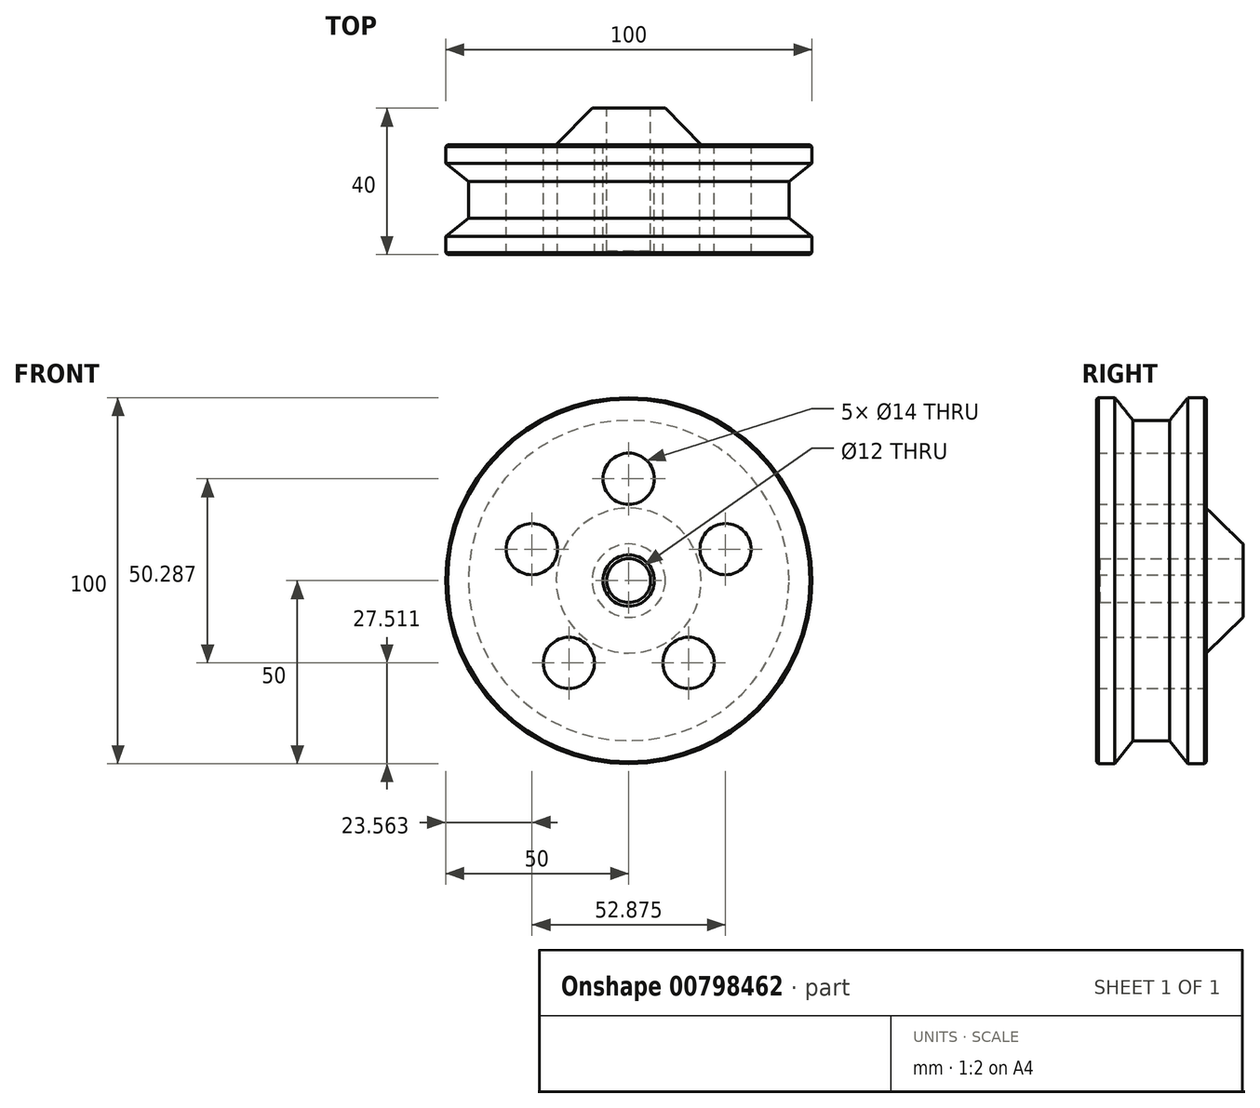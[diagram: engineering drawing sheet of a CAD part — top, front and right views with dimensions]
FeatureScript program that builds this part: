
annotation { "Feature Type Name" : "Feature", "Feature Type Description" : "" }
export const myFeature = defineFeature(function(context is Context, id is Id, definition is map)
    precondition{}
    {
        {
            var Q0;
            Q0=qCreatedBy(makeId("Top.planeOp"),FACE);
            var sketch = newSketch(context, id + "F0", { "sketchPlane" : qUnion([Q0])});
            skLineSegment(sketch, "E0.top", {"start": v(0, -40) * mm, "end": v(-50, -40) * mm});
            skLineSegment(sketch, "E0.left", {"start": v(0, 0) * mm, "end": v(0, -40) * mm});
            skLineSegment(sketch, "E1", {"start": v(-50, -10) * mm, "end": v(-50, -15) * mm});
            skLineSegment(sketch, "E2", {"start": v(-50, -15) * mm, "end": v(-43.76, -20) * mm});
            skLineSegment(sketch, "E3", {"start": v(-43.76, -20) * mm, "end": v(-43.76, -30) * mm});
            skLineSegment(sketch, "E4", {"start": v(-43.76, -30) * mm, "end": v(-50, -35) * mm});
            skLineSegment(sketch, "E5", {"start": v(-50, -40) * mm, "end": v(-50, -35) * mm});
            skLineSegment(sketch, "E6", {"start": v(0, 0) * mm, "end": v(-10, 0) * mm});
            skLineSegment(sketch, "E7", {"start": v(-10, 0) * mm, "end": v(-19.8, -10) * mm});
            skLineSegment(sketch, "E8", {"start": v(-19.8, -10) * mm, "end": v(-50, -10) * mm});
            skSolve(sketch);
        }
        {
            var Q0;
            Q0=makeQuery(id+"F0.imprint","IMPRINT",FACE,{"disambiguationData":[TD([[makeQuery(id+"F0.imprint","IMPRINT",EDGE,{"derivedFrom":sQuery(id+"F0.wireOp",EDGE,"E0.top")}),-1.0]])]});
            var Q1;
            Q1=sQuery(id+"F0.wireOp",EDGE,"E0.left");
            revolve(context, id + "F1", {"surfaceOperationType" : NewSurfaceOperationType.NEW, "entities" : qUnion([Q0]), "axis" : qUnion([Q1]), "revolveType" : RevolveType.FULL});
        }
        {
            var Q0;
            Q0=makeQuery(id+"F1.opRevolve","SWEPT_FACE",FACE,{"disambiguationData":[OSD([sQuery(id+"F0.wireOp",EDGE,"E6")])]});
            var sketch = newSketch(context, id + "F2", { "sketchPlane" : qUnion([Q0])});
            skCircle(sketch, "E9", {"center": v(0, 0) * mm, "radius": 6 * mm});
            skSolve(sketch);
        }
        {
            var Q0;
            Q0=makeQuery(id+"F2.imprint","IMPRINT",FACE,{"disambiguationData":[TD([[makeQuery(id+"F2.imprint","IMPRINT",EDGE,{"derivedFrom":sQuery(id+"F2.wireOp",EDGE,"E9")}),1.0]])]});
            extrude(context, id + "F3", {"entities" : qUnion([Q0]), "operationType" : NewBodyOperationType.REMOVE, "endBound" : BoundingType.THROUGH_ALL, "oppositeDirection" : true, "depth" : 25 * mm, "offsetDistance" : 25 * mm});
        }
        {
            var Q0;
            Q0=makeQuery(id+"F1.opRevolve","SWEPT_FACE",FACE,{"disambiguationData":[OSD([sQuery(id+"F0.wireOp",EDGE,"E8")])]});
            var sketch = newSketch(context, id + "F4", { "sketchPlane" : qUnion([Q0])});
            skCircle(sketch, "E10", {"center": v(0, 27.8) * mm, "radius": 7 * mm});
            skCircle(sketch, "E11.1.0", {"center": v(-26.44, 8.6) * mm, "radius": 7 * mm});
            skCircle(sketch, "E11.2.0", {"center": v(-16.34, -22.49) * mm, "radius": 7 * mm});
            skCircle(sketch, "E11.3.0", {"center": v(16.34, -22.49) * mm, "radius": 7 * mm});
            skCircle(sketch, "E11.4.0", {"center": v(26.44, 8.6) * mm, "radius": 7 * mm});
            skPoint(sketch, "E11.center", {"position": v(0, 0) * mm});
            skSolve(sketch);
        }
        {
            var Q0;
            Q0=makeQuery(id+"F4.imprint","IMPRINT",FACE,{"disambiguationData":[TD([[makeQuery(id+"F4.imprint","IMPRINT",EDGE,{"derivedFrom":sQuery(id+"F4.wireOp",EDGE,"E10")}),1.0]])]});
            var Q1;
            Q1=makeQuery(id+"F4.imprint","IMPRINT",FACE,{"disambiguationData":[TD([[makeQuery(id+"F4.imprint","IMPRINT",EDGE,{"derivedFrom":sQuery(id+"F4.wireOp",EDGE,"E11.4.0")}),1.0]])]});
            var Q2;
            Q2=makeQuery(id+"F4.imprint","IMPRINT",FACE,{"disambiguationData":[TD([[makeQuery(id+"F4.imprint","IMPRINT",EDGE,{"derivedFrom":sQuery(id+"F4.wireOp",EDGE,"E11.3.0")}),1.0]])]});
            var Q3;
            Q3=makeQuery(id+"F4.imprint","IMPRINT",FACE,{"disambiguationData":[TD([[makeQuery(id+"F4.imprint","IMPRINT",EDGE,{"derivedFrom":sQuery(id+"F4.wireOp",EDGE,"E11.2.0")}),1.0]])]});
            var Q4;
            Q4=makeQuery(id+"F4.imprint","IMPRINT",FACE,{"disambiguationData":[TD([[makeQuery(id+"F4.imprint","IMPRINT",EDGE,{"derivedFrom":sQuery(id+"F4.wireOp",EDGE,"E11.1.0")}),1.0]])]});
            extrude(context, id + "F5", {"entities" : qUnion([Q0, Q1, Q2, Q3, Q4]), "operationType" : NewBodyOperationType.REMOVE, "oppositeDirection" : true, "depth" : 30 * mm, "offsetDistance" : 25 * mm});
        }
        {
            var Q0;
            Q0=makeQuery(id+"F1.opRevolve","SWEPT_EDGE",EDGE,{"disambiguationData":[OSD([sQuery(id+"F0.wireOp",EDGE,"E0.top"),sQuery(id+"F0.wireOp",EDGE,"E5")])]});
            var Q1;
            Q1=makeQuery(id+"F1.opRevolve","SWEPT_EDGE",EDGE,{"disambiguationData":[OSD([sQuery(id+"F0.wireOp",EDGE,"E1"),sQuery(id+"F0.wireOp",EDGE,"E8")])]});
            chamfer(context, id + "F6", {"entities" : qUnion([Q0, Q1]), "width" : 0.5 * mm, "tangentPropagation" : true});
        }
        {
            var Q0;
            Q0=makeQuery(id+"F5.boolean.opBoolean","COPY",EDGE,{"derivedFrom":makeQuery(id+"F5.opExtrude","CAP_EDGE",EDGE,{"disambiguationData":[OSD([sQuery(id+"F4.wireOp",EDGE,"E10")])],"isStart":true})});
            var Q1;
            Q1=makeQuery(id+"F5.boolean.opBoolean","COPY",EDGE,{"derivedFrom":makeQuery(id+"F5.opExtrude","CAP_EDGE",EDGE,{"disambiguationData":[OSD([sQuery(id+"F4.wireOp",EDGE,"E11.4.0")])],"isStart":true})});
            var Q2;
            Q2=makeQuery(id+"F5.boolean.opBoolean","COPY",EDGE,{"derivedFrom":makeQuery(id+"F5.opExtrude","CAP_EDGE",EDGE,{"disambiguationData":[OSD([sQuery(id+"F4.wireOp",EDGE,"E11.3.0")])],"isStart":true})});
            var Q3;
            Q3=makeQuery(id+"F5.boolean.opBoolean","COPY",EDGE,{"derivedFrom":makeQuery(id+"F5.opExtrude","CAP_EDGE",EDGE,{"disambiguationData":[OSD([sQuery(id+"F4.wireOp",EDGE,"E11.2.0")])],"isStart":true})});
            var Q4;
            Q4=makeQuery(id+"F5.boolean.opBoolean","COPY",EDGE,{"derivedFrom":makeQuery(id+"F5.opExtrude","CAP_EDGE",EDGE,{"disambiguationData":[OSD([sQuery(id+"F4.wireOp",EDGE,"E11.1.0")])],"isStart":true})});
            var Q5;
            Q5=makeQuery(id+"F5.boolean.opBoolean","COPY",EDGE,{"derivedFrom":makeQuery(id+"F5.opExtrude","CAP_EDGE",EDGE,{"disambiguationData":[OSD([sQuery(id+"F4.wireOp",EDGE,"E11.3.0")])],"isStart":false})});
            var Q6;
            Q6=makeQuery(id+"F5.boolean.opBoolean","COPY",EDGE,{"derivedFrom":makeQuery(id+"F5.opExtrude","CAP_EDGE",EDGE,{"disambiguationData":[OSD([sQuery(id+"F4.wireOp",EDGE,"E11.4.0")])],"isStart":false})});
            var Q7;
            Q7=makeQuery(id+"F5.boolean.opBoolean","COPY",EDGE,{"derivedFrom":makeQuery(id+"F5.opExtrude","CAP_EDGE",EDGE,{"disambiguationData":[OSD([sQuery(id+"F4.wireOp",EDGE,"E11.1.0")])],"isStart":false})});
            var Q8;
            Q8=makeQuery(id+"F5.boolean.opBoolean","COPY",EDGE,{"derivedFrom":makeQuery(id+"F5.opExtrude","CAP_EDGE",EDGE,{"disambiguationData":[OSD([sQuery(id+"F4.wireOp",EDGE,"E11.2.0")])],"isStart":false})});
            var Q9;
            Q9=makeQuery(id+"F3.boolean.opBoolean","INTERSECT",EDGE,{"derivedFrom":[makeQuery(id+"F1.opRevolve","SWEPT_FACE",FACE,{"disambiguationData":[OSD([sQuery(id+"F0.wireOp",EDGE,"E0.top")])]}),makeQuery(id+"F3.opExtrude","SWEPT_FACE",FACE,{"disambiguationData":[OSD([sQuery(id+"F2.wireOp",EDGE,"E9")])]})]});
            var Q10;
            Q10=makeQuery(id+"F5.boolean.opBoolean","COPY",EDGE,{"derivedFrom":makeQuery(id+"F5.opExtrude","CAP_EDGE",EDGE,{"disambiguationData":[OSD([sQuery(id+"F4.wireOp",EDGE,"E10")])],"isStart":false})});
            chamfer(context, id + "F7", {"entities" : qUnion([Q0, Q1, Q2, Q3, Q4, Q5, Q6, Q7, Q8, Q9, Q10]), "width" : 1 * mm, "tangentPropagation" : true});
        }
    });
